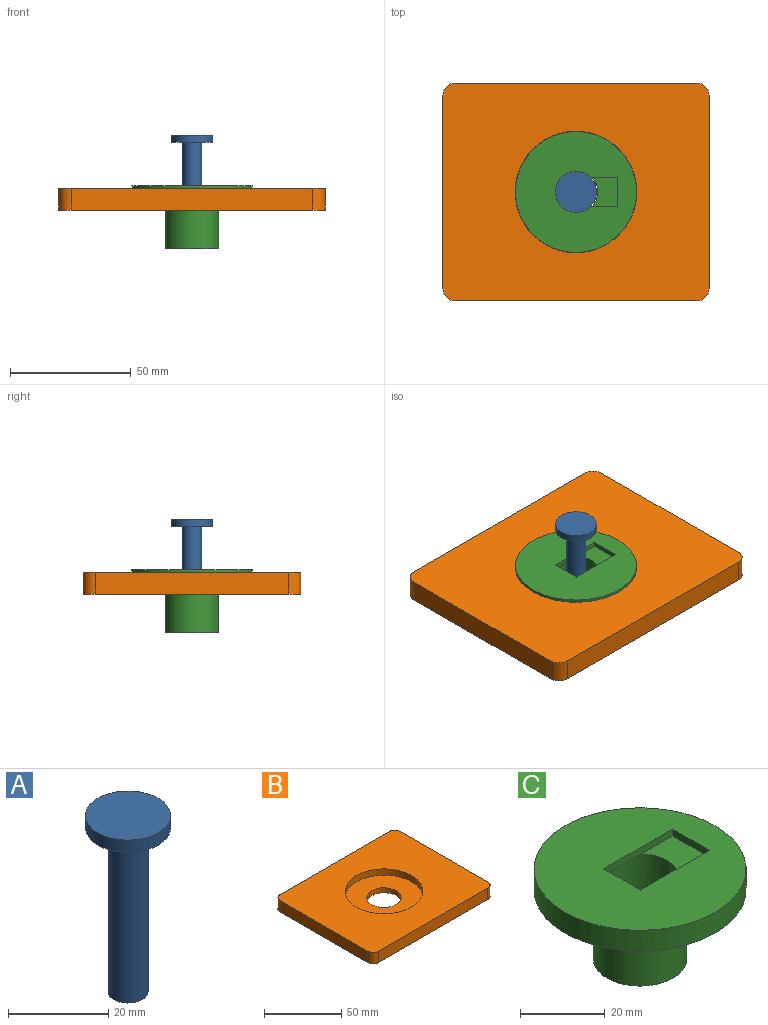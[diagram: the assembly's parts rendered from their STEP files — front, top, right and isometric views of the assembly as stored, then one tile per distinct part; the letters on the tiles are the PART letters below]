
ASSEMBLY  parts=3 mates=2
PART A: 5 faces, bbox 17x17x43 mm
  f0: cylinder r=8.5mm len=17mm, axis (0,0,1), area 160.2mm2, adj f1,f2
  f1: plane 17x17mm, normal (0,0,-1), area 176.7mm2, adj f0,f3
  f2: plane 17x17mm, normal (0,0,1), area 227mm2, adj f0
  f3: cylinder r=4mm len=40mm, axis (0,0,1), area 1005.3mm2, adj f1,f4
  f4: plane 8x8mm, normal (0,0,-1), area 50.3mm2, adj f3
PART B: 13 faces, bbox 110x90x9 mm
  f0: plane 100x9mm, normal (0,1,0), area 900mm2, adj f4,f5,f9,f12
  f1: plane 80x9mm, normal (-1,0,0), area 720mm2, adj f4,f5,f9,f10
  f2: plane 100x9mm, normal (0,-1,0), area 900mm2, adj f4,f5,f10,f11
  f3: plane 80x9mm, normal (1,0,0), area 720mm2, adj f4,f5,f11,f12
  f4: plane 110x90mm, normal (0,0,1), area 7891.4mm2, adj f0,f1,f2,f3,f6,f9,f10,f11
  f5: plane 110x90mm, normal (0,0,-1), area 9491.5mm2, adj f0,f1,f2,f3,f8,f9,f10,f11
  f6: cylinder r=25.15mm len=50.3mm, axis (0,0,1), area 790.1mm2, adj f4,f7
  f7: plane 50.3x50.3mm, normal (0,0,1), area 1600.1mm2, adj f6,f8
  f8: cylinder r=11.1mm len=22.2mm, axis (0,0,1), area 279mm2, adj f5,f7
  f9: cylinder r=5mm len=9mm, axis (0,0,1), area 70.7mm2, adj f0,f1,f4,f5
  f10: cylinder r=5mm len=9mm, axis (0,0,-1), area 70.7mm2, adj f1,f2,f4,f5
  f11: cylinder r=5mm len=9mm, axis (0,0,1), area 70.7mm2, adj f2,f3,f4,f5
  f12: cylinder r=5mm len=9mm, axis (0,0,-1), area 70.7mm2, adj f0,f3,f4,f5
PART C: 12 faces, bbox 50x50x26 mm
  f0: plane 12.3x10.43mm, normal (0,0,1), area 107.8mm2, adj f1,f6,f8,f9
  f1: cylinder r=9mm len=24mm, axis (0,0,-1), area 1357.2mm2, adj f0,f3,f11
  f2: cylinder r=11mm len=22mm, axis (0,0,-1), area 1382.3mm2, adj f3,f5
  f3: plane 22x22mm, normal (0,0,-1), area 125.7mm2, adj f1,f2
  f4: cylinder r=25mm len=50mm, axis (0,0,-1), area 942.5mm2, adj f5,f10
  f5: plane 50x50mm, normal (0,0,-1), area 1583.4mm2, adj f2,f4
  f6: plane 23x2mm, normal (0,1,0), area 46mm2, adj f0,f7,f9,f10,f11
  f7: plane 12.3x2mm, normal (1,0,0), area 24.6mm2, adj f6,f8,f10,f11
  f8: plane 23x2mm, normal (0,-1,0), area 46mm2, adj f0,f7,f9,f10,f11
  f9: plane 12.3x2mm, normal (-1,0,0), area 24.6mm2, adj f0,f6,f8,f10
  f10: plane 50x50mm, normal (0,0,1), area 1680.6mm2, adj f4,f6,f7,f8,f9
  f11: plane 18x15.57mm, normal (0,0,-1), area 79.3mm2, adj f1,f6,f7,f8
PLACE A t=(-29.06,-3.08,53.55)mm
PLACE B t=(-29.06,-3.08,7.55)mm
PLACE C t=(-29.06,-3.08,6.55)mm
MATE planar C.f4 <-> B.f6  axis (0,0,-1) through (-29.06,-3.08,26.55)mm
MATE revolute A.f3 <-> C.f1  axis (0,0,1) through (-29.06,-3.08,30.55)mm
